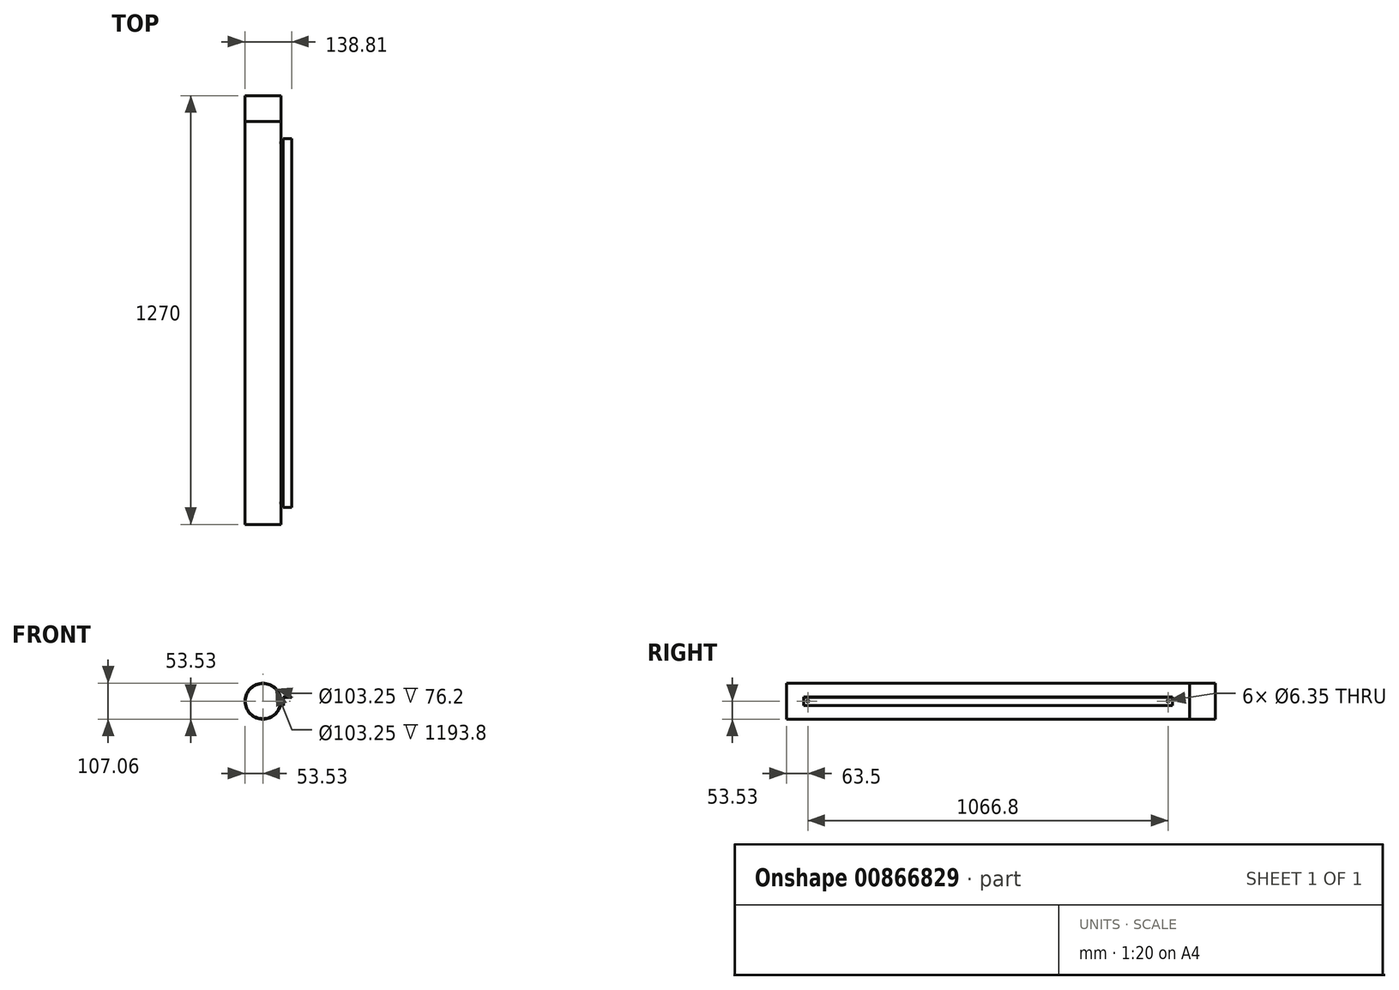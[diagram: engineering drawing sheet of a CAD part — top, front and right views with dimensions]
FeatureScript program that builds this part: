
annotation { "Feature Type Name" : "Feature", "Feature Type Description" : "" }
export const myFeature = defineFeature(function(context is Context, id is Id, definition is map)
    precondition{}
    {
        {
            var Q0;
            Q0=qCreatedBy(makeId("Front.planeOp"),FACE);
            var sketch = newSketch(context, id + "F0", { "sketchPlane" : qUnion([Q0])});
            skCircle(sketch, "E0", {"center": v(0, 0) * mm, "radius": 53.53 * mm});
            skCircle(sketch, "E1.0", {"center": v(0, 0) * mm, "radius": 51.63 * mm});
            skSolve(sketch);
        }
        {
            var Q0;
            Q0=makeQuery(id+"F0.imprint","IMPRINT",FACE,{"disambiguationData":[TD([[makeQuery(id+"F0.imprint","IMPRINT",EDGE,{"derivedFrom":sQuery(id+"F0.wireOp",EDGE,"E0")}),1.0]])]});
            extrude(context, id + "F1", {"entities" : qUnion([Q0]), "depth" : 1193.8 * mm, "offsetDistance" : 25.4 * mm});
        }
        {
            var Q0;
            Q0=makeQuery(id+"F1.opExtrude","CAP_FACE",FACE,{"disambiguationData":[OSD([sQuery(id+"F0.wireOp",EDGE,"E0"),sQuery(id+"F0.wireOp",EDGE,"E1.0")])],"isStart":true});
            extrude(context, id + "F2", {"entities" : qUnion([Q0]), "depth" : 76.2 * mm, "offsetDistance" : 25.4 * mm});
        }
        {
            var Q0;
            Q0=qCreatedBy(makeId("Right.planeOp"),FACE);
            var sketch = newSketch(context, id + "F3", { "sketchPlane" : qUnion([Q0])});
            skLineSegment(sketch, "E2.0", {"start": v(-1193.8, -53.53) * mm, "end": v(-1193.8, 53.53) * mm, "construction": true});
            skLineSegment(sketch, "E3", {"start": v(-1193.8, 0) * mm, "end": v(-1130.3, 0) * mm, "construction": true});
            skLineSegment(sketch, "E4.0", {"start": v(0, -53.53) * mm, "end": v(0, 53.53) * mm, "construction": true});
            skLineSegment(sketch, "E5", {"start": v(0, 0) * mm, "end": v(-63.5, 0) * mm, "construction": true});
            skSolve(sketch);
        }
        {
            var Q0;
            Q0=sQuery(id+"F3.wireOp",VERTEX,"E3.end");
            var Q1;
            Q1=makeQuery(id+"F1.opExtrude","SWEPT_BODY",BODY,{"disambiguationData":[OSD([sQuery(id+"F0.wireOp",EDGE,"E0"),sQuery(id+"F0.wireOp",EDGE,"E1.0")])]});
            hole(context, id + "F4", {"style" : HoleStyle.SIMPLE, "endStyle" : HoleEndStyle.THROUGH, "holeDiameter" : 6.35 * mm, "majorDiameter" : 6.35 * mm, "isTappedThrough" : true, "tappedDepth" : 12.7 * mm, "tapClearance" : 3, "locations" : qUnion([Q0]), "scope" : qUnion([Q1])});
        }
        {
            var Q0;
            Q0=sQuery(id+"F3.wireOp",VERTEX,"E3.end");
            var Q1;
            Q1=makeQuery(id+"F1.opExtrude","SWEPT_BODY",BODY,{"disambiguationData":[OSD([sQuery(id+"F0.wireOp",EDGE,"E0"),sQuery(id+"F0.wireOp",EDGE,"E1.0")])]});
            hole(context, id + "F5", {"style" : HoleStyle.SIMPLE, "endStyle" : HoleEndStyle.THROUGH, "oppositeDirection" : true, "holeDiameter" : 6.35 * mm, "majorDiameter" : 6.35 * mm, "isTappedThrough" : true, "tappedDepth" : 12.7 * mm, "tapClearance" : 3, "locations" : qUnion([Q0]), "scope" : qUnion([Q1])});
        }
        {
            var Q0;
            Q0=sQuery(id+"F3.wireOp",VERTEX,"E5.end");
            var Q1;
            Q1=makeQuery(id+"F1.opExtrude","SWEPT_BODY",BODY,{"disambiguationData":[OSD([sQuery(id+"F0.wireOp",EDGE,"E0"),sQuery(id+"F0.wireOp",EDGE,"E1.0")])]});
            hole(context, id + "F6", {"style" : HoleStyle.SIMPLE, "endStyle" : HoleEndStyle.THROUGH, "holeDiameter" : 6.35 * mm, "majorDiameter" : 6.35 * mm, "isTappedThrough" : true, "tappedDepth" : 12.7 * mm, "tapClearance" : 3, "locations" : qUnion([Q0]), "scope" : qUnion([Q1])});
        }
        {
            var Q0;
            Q0=sQuery(id+"F3.wireOp",VERTEX,"E5.end");
            var Q1;
            Q1=makeQuery(id+"F1.opExtrude","SWEPT_BODY",BODY,{"disambiguationData":[OSD([sQuery(id+"F0.wireOp",EDGE,"E0"),sQuery(id+"F0.wireOp",EDGE,"E1.0")])]});
            hole(context, id + "F7", {"style" : HoleStyle.SIMPLE, "endStyle" : HoleEndStyle.THROUGH, "oppositeDirection" : true, "holeDiameter" : 6.35 * mm, "majorDiameter" : 6.35 * mm, "isTappedThrough" : true, "tappedDepth" : 12.7 * mm, "tapClearance" : 3, "locations" : qUnion([Q0]), "scope" : qUnion([Q1])});
        }
        {
            var Q0;
            Q0=sQuery(id+"F3.wireOp",VERTEX,"E3.end");
            var Q1;
            Q1=sQuery(id+"F3.wireOp",EDGE,"E3");
            cPlane(context, id + "F8", {"entities" : qUnion([Q0, Q1]), "cplaneType" : CPlaneType.CURVE_POINT, "offset" : 25.4 * mm, "width" : 152.4 * mm, "height" : 152.4 * mm});
        }
        {
            var Q0;
            Q0=sQuery(id+"F3.wireOp",VERTEX,"E5.end");
            var Q1;
            Q1=sQuery(id+"F3.wireOp",EDGE,"E5");
            cPlane(context, id + "F9", {"entities" : qUnion([Q0, Q1]), "cplaneType" : CPlaneType.CURVE_POINT, "offset" : 25.4 * mm, "width" : 152.4 * mm, "height" : 152.4 * mm});
        }
        {
            var Q0;
            Q0=qCreatedBy(id+"F9.planeOp",FACE);
            var sketch = newSketch(context, id + "F10", { "sketchPlane" : qUnion([Q0])});
            skLineSegment(sketch, "E6", {"start": v(59.88, 12.7) * mm, "end": v(59.88, -12.7) * mm});
            skLineSegment(sketch, "E7", {"start": v(59.88, -12.7) * mm, "end": v(61.47, -12.7) * mm});
            skLineSegment(sketch, "E8", {"start": v(61.47, -12.7) * mm, "end": v(61.47, 11.11) * mm});
            skLineSegment(sketch, "E9", {"start": v(61.47, 11.11) * mm, "end": v(85.28, 11.11) * mm});
            skLineSegment(sketch, "E10", {"start": v(85.28, 11.11) * mm, "end": v(85.28, 12.7) * mm});
            skLineSegment(sketch, "E11", {"start": v(85.28, 12.7) * mm, "end": v(59.88, 12.7) * mm});
            skPoint(sketch, "E12", {"position": v(59.88, 0) * mm});
            skSolve(sketch);
        }
        {
            var Q0;
            Q0=makeQuery(id+"F10.imprint","IMPRINT",FACE,{"disambiguationData":[TD([[makeQuery(id+"F10.imprint","IMPRINT",EDGE,{"derivedFrom":sQuery(id+"F10.wireOp",EDGE,"E6")}),1.0]])]});
            var Q1;
            Q1=qCreatedBy(id+"F8.planeOp",FACE);
            extrude(context, id + "F11", {"entities" : qUnion([Q0]), "endBound" : BoundingType.UP_TO_SURFACE, "depth" : 25.4 * mm, "endBoundEntityFace" : qUnion([Q1]), "offsetDistance" : 25.4 * mm});
        }
        {
            var Q0;
            Q0=makeQuery(id+"F11.opExtrude","CAP_FACE",FACE,{"disambiguationData":[OSD([sQuery(id+"F10.wireOp",EDGE,"E6"),sQuery(id+"F10.wireOp",EDGE,"E7"),sQuery(id+"F10.wireOp",EDGE,"E8"),sQuery(id+"F10.wireOp",EDGE,"E9"),sQuery(id+"F10.wireOp",EDGE,"E10"),sQuery(id+"F10.wireOp",EDGE,"E11")])],"isStart":false});
            extrude(context, id + "F12", {"entities" : qUnion([Q0]), "operationType" : NewBodyOperationType.ADD, "depth" : 12.7 * mm, "offsetDistance" : 25.4 * mm});
        }
        {
            var Q0;
            Q0=makeQuery(id+"F11.opExtrude","CAP_FACE",FACE,{"disambiguationData":[OSD([sQuery(id+"F10.wireOp",EDGE,"E6"),sQuery(id+"F10.wireOp",EDGE,"E7"),sQuery(id+"F10.wireOp",EDGE,"E8"),sQuery(id+"F10.wireOp",EDGE,"E9"),sQuery(id+"F10.wireOp",EDGE,"E10"),sQuery(id+"F10.wireOp",EDGE,"E11")])],"isStart":true});
            extrude(context, id + "F13", {"entities" : qUnion([Q0]), "operationType" : NewBodyOperationType.ADD, "depth" : 12.7 * mm, "offsetDistance" : 25.4 * mm});
        }
        {
            var Q0;
            Q0=sQuery(id+"F3.wireOp",VERTEX,"E3.end");
            var Q1;
            Q1=makeQuery(id+"F11.opExtrude","SWEPT_BODY",BODY,{"disambiguationData":[OSD([sQuery(id+"F10.wireOp",EDGE,"E6"),sQuery(id+"F10.wireOp",EDGE,"E7"),sQuery(id+"F10.wireOp",EDGE,"E8"),sQuery(id+"F10.wireOp",EDGE,"E9"),sQuery(id+"F10.wireOp",EDGE,"E10"),sQuery(id+"F10.wireOp",EDGE,"E11")])]});
            hole(context, id + "F14", {"style" : HoleStyle.SIMPLE, "endStyle" : HoleEndStyle.THROUGH, "oppositeDirection" : true, "holeDiameter" : 6.35 * mm, "majorDiameter" : 6.35 * mm, "isTappedThrough" : true, "tappedDepth" : 12.7 * mm, "tapClearance" : 3, "locations" : qUnion([Q0]), "scope" : qUnion([Q1])});
        }
        {
            var Q0;
            Q0=sQuery(id+"F3.wireOp",VERTEX,"E5.end");
            var Q1;
            Q1=makeQuery(id+"F11.opExtrude","SWEPT_BODY",BODY,{"disambiguationData":[OSD([sQuery(id+"F10.wireOp",EDGE,"E6"),sQuery(id+"F10.wireOp",EDGE,"E7"),sQuery(id+"F10.wireOp",EDGE,"E8"),sQuery(id+"F10.wireOp",EDGE,"E9"),sQuery(id+"F10.wireOp",EDGE,"E10"),sQuery(id+"F10.wireOp",EDGE,"E11")])]});
            hole(context, id + "F15", {"style" : HoleStyle.SIMPLE, "endStyle" : HoleEndStyle.THROUGH, "oppositeDirection" : true, "holeDiameter" : 6.35 * mm, "majorDiameter" : 6.35 * mm, "isTappedThrough" : true, "tappedDepth" : 12.7 * mm, "tapClearance" : 3, "locations" : qUnion([Q0]), "scope" : qUnion([Q1])});
        }
    });
